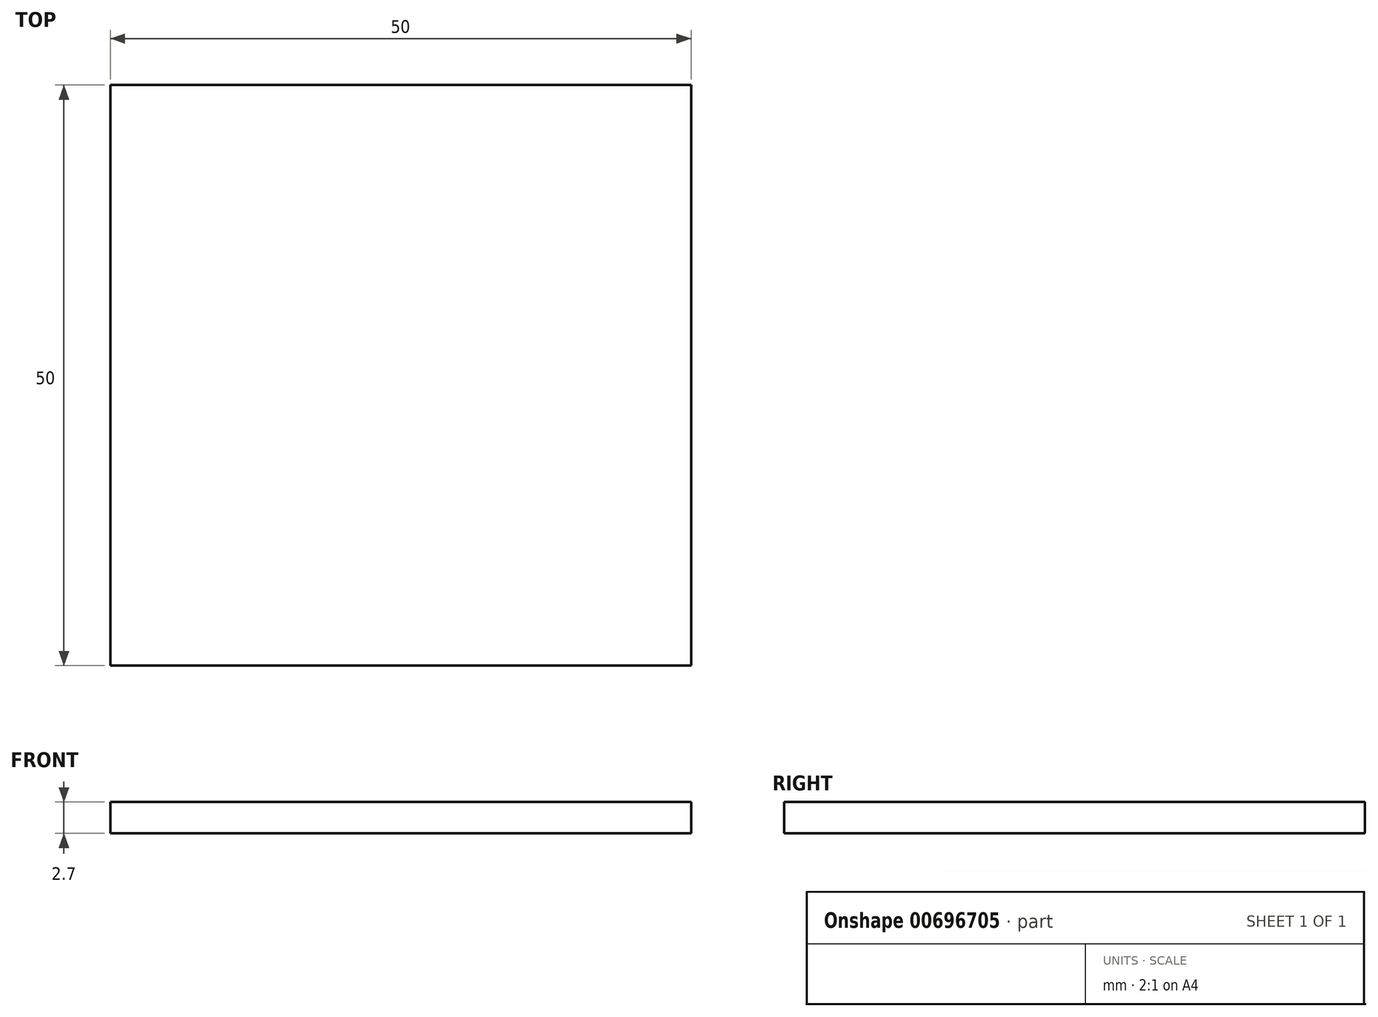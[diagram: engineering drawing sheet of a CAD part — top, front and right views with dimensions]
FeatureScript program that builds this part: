
annotation { "Feature Type Name" : "Feature", "Feature Type Description" : "" }
export const myFeature = defineFeature(function(context is Context, id is Id, definition is map)
    precondition{}
    {
        {
            var Q0;
            Q0=qCreatedBy(makeId("Top.planeOp"),FACE);
            var sketch = newSketch(context, id + "F0", { "sketchPlane" : qUnion([Q0])});
            skLineSegment(sketch, "E0.bottom", {"start": v(25, -25) * mm, "end": v(-25, -25) * mm});
            skLineSegment(sketch, "E0.top", {"start": v(25, 25) * mm, "end": v(-25, 25) * mm});
            skLineSegment(sketch, "E0.left", {"start": v(25, -25) * mm, "end": v(25, 25) * mm});
            skLineSegment(sketch, "E0.right", {"start": v(-25, -25) * mm, "end": v(-25, 25) * mm});
            skPoint(sketch, "E0.middle", {"position": v(0, 0) * mm});
            skSolve(sketch);
        }
        {
            var Q0;
            Q0=makeQuery(id+"F0.imprint","IMPRINT",FACE,{"disambiguationData":[TD([[makeQuery(id+"F0.imprint","IMPRINT",EDGE,{"derivedFrom":sQuery(id+"F0.wireOp",EDGE,"E0.bottom")}),-1.0]])]});
            extrude(context, id + "F1", {"entities" : qUnion([Q0]), "depth" : 2.7 * mm, "offsetDistance" : 25 * mm});
        }
    });
